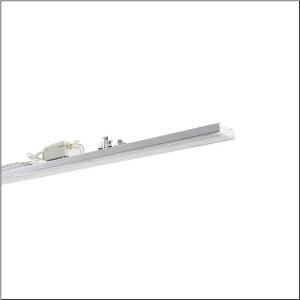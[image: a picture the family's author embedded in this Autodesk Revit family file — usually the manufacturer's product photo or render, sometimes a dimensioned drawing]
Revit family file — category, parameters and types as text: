
# Revit family: licross_r__21_recessed_ho_52te12dv4l2m3c_c3a2
name_source: partatom
category: Lighting Fixtures
units: mm (PartAtom-declared; Revit-internal decimal feet)

## family parameters
Cut with Voids When Loaded = No
Host = Face
Light Source = No
Part Type = Normal
Room Calculation Point = No
Round Connector Dimension = Use Diameter
Shared = No

## types (1)
- --- (1 x LED, 910 lm, 6.4 W, 4000K)
    Apparent Load = 6 VA
    CIE Flux Codes = 69 91 98 100 100
    Color Rendering = 80
    Color Temperature = 4000K
    Default Elevation = 1800 mm
    Description = Licross® 21 Recessed HO, luminaire insert, of sheet steel, galvanised, coil coated, white, length: 2.250mm, width: 66mm, height: 67mm, LED rated luminous flux: 22.710lm, light colour: 840, control gear: DALI 2, with plug, 6-pole, with phase selection, for trunking rail, 14-core, mains connection: 220..240V, AC, 50/60Hz, rated input power: 129W, for trunking rail, 14-core, halogen-free wiring, for emergency light function, converter,control gear: single battery element, battery: LiFeP04, 9Ah, primary optical cover: cover, of PMMA, light emission: direct distribution, primary light characteristic: symmetric, protection rating (complete): IP54, insulation class (complete): insulation class I (protective earthing), certification: CE, UKCA, protection symbol: D if used in an environment with non-conductive dust loads with corresponding accessories, impact resistance: IK06, permissible ambient temperature for indoor applications: +5..+30°C, standard: EN 60598-2-22, LABS conformity tested according to VDMA 24364:2018-05, reducing of maximum allowable ambient temperature of 5°C with ceiling mounting, corresponds to IFS (International Featured Standards) requirements for safety and quality in the food industry, packaging unit: 1 piece
    Height = 58 mm
    Lamp = 1 x LED
    Lamp Light Flux = 910 lm
    Lamp Power = 6.4 W
    Lamp count = 1
    Length = 2250 mm
    Luminous efficacy = 142 lm/W
    Manufacturer = Siteco
    ModVariant = No
    Model = 52TE12DV4L2M3C
    Mounting Place = Ceiling
    Mounting Type = Pendant
    Number of Poles = 1
    OnlyDefault = Yes
    Power Factor = 1
    Product Name = Licross® 21 Recessed HO
    Product group = luminaire insert
    ProductGroupID = 901
    Protection Class = Protection class I
    Protection Degree = IP 54
    RLX_Detail_Level = 1
    RLX_Emergency_Light_Flux = 0 lm
    RLX_Emergency_Type = 0
    RLX_Emergency_Type_DB = No
    RlxData = <blob elided: 29705 chars, md5=94d57177>
    Socket = socket
    Standby Power = 0 W
    System Light Flux = 910 lm
    System Power = 6 W
    Type Comments = : emergency light operation: 3 h
    Type Image = l_1296930.jpg
    URL = http://relux.com
    VarID = @adj_039457
    Voltage = 0 V
    Weight = 0.00 kg
    Width = 66 mm

## geometry (parser evidence)
native form markers: Blend x4, Sweep x10
no freeform markers — native parametric forms only
